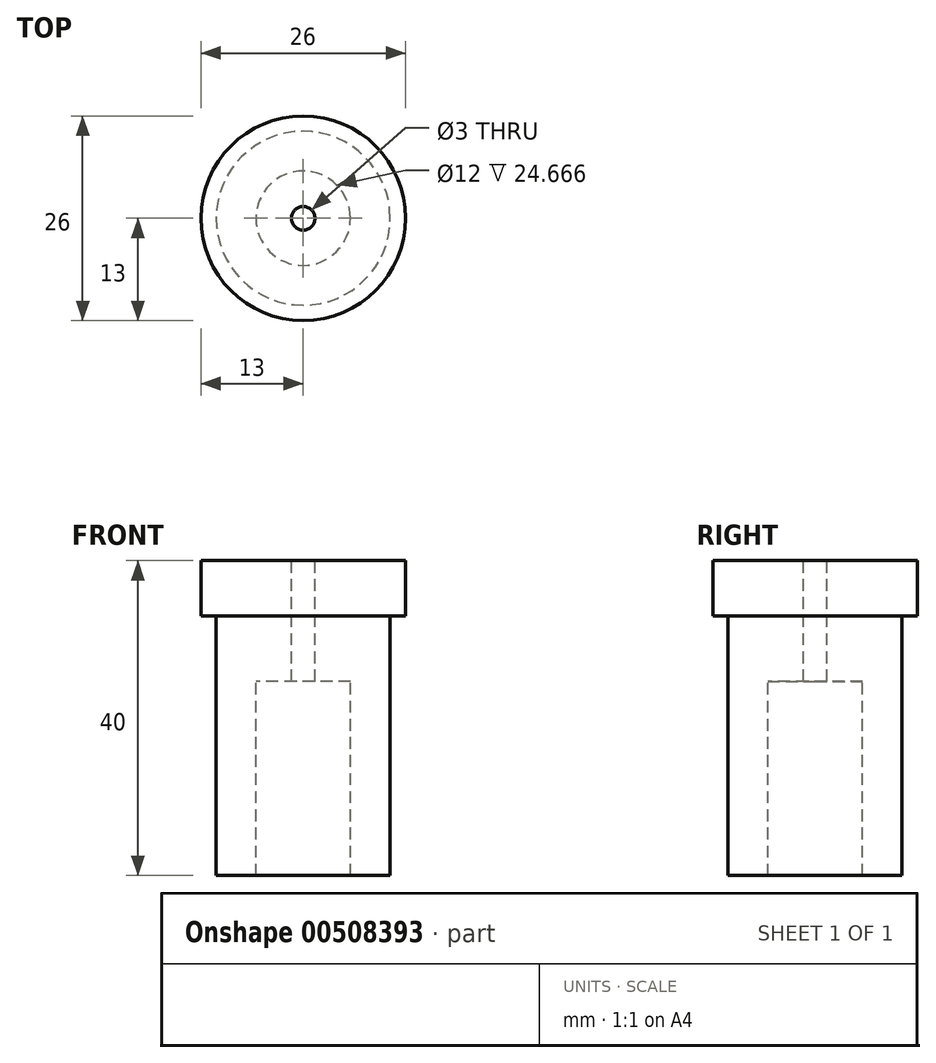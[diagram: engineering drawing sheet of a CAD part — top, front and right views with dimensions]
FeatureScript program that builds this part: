
annotation { "Feature Type Name" : "Feature", "Feature Type Description" : "" }
export const myFeature = defineFeature(function(context is Context, id is Id, definition is map)
    precondition{}
    {
        {
            var Q0;
            Q0=qCreatedBy(makeId("Front.planeOp"),FACE);
            var sketch = newSketch(context, id + "F0", { "sketchPlane" : qUnion([Q0])});
            skLineSegment(sketch, "E0", {"start": v(1.5, 40) * mm, "end": v(1.5, 24.67) * mm});
            skLineSegment(sketch, "E1", {"start": v(1.5, 40) * mm, "end": v(13, 40) * mm});
            skLineSegment(sketch, "E2", {"start": v(13, 40) * mm, "end": v(13, 33) * mm});
            skLineSegment(sketch, "E3", {"start": v(13, 33) * mm, "end": v(11.05, 33) * mm});
            skLineSegment(sketch, "E4", {"start": v(11.05, 33) * mm, "end": v(11.05, 0) * mm});
            skLineSegment(sketch, "E5", {"start": v(1.5, 24.67) * mm, "end": v(6, 24.67) * mm});
            skLineSegment(sketch, "E6", {"start": v(6, 24.67) * mm, "end": v(6, 0) * mm});
            skLineSegment(sketch, "E7", {"start": v(6, 0) * mm, "end": v(11.05, 0) * mm});
            skLineSegment(sketch, "E8", {"start": v(0, 49.46) * mm, "end": v(0, -6.58) * mm, "construction": true});
            skSolve(sketch);
        }
        {
            var Q0;
            Q0 = qSketchRegion(id + "F0", true);
            var Q1;
            Q1=sQuery(id+"F0.wireOp",EDGE,"E8");
            revolve(context, id + "F1", {"entities" : qUnion([Q0]), "axis" : qUnion([Q1]), "revolveType" : RevolveType.FULL});
        }
    });
